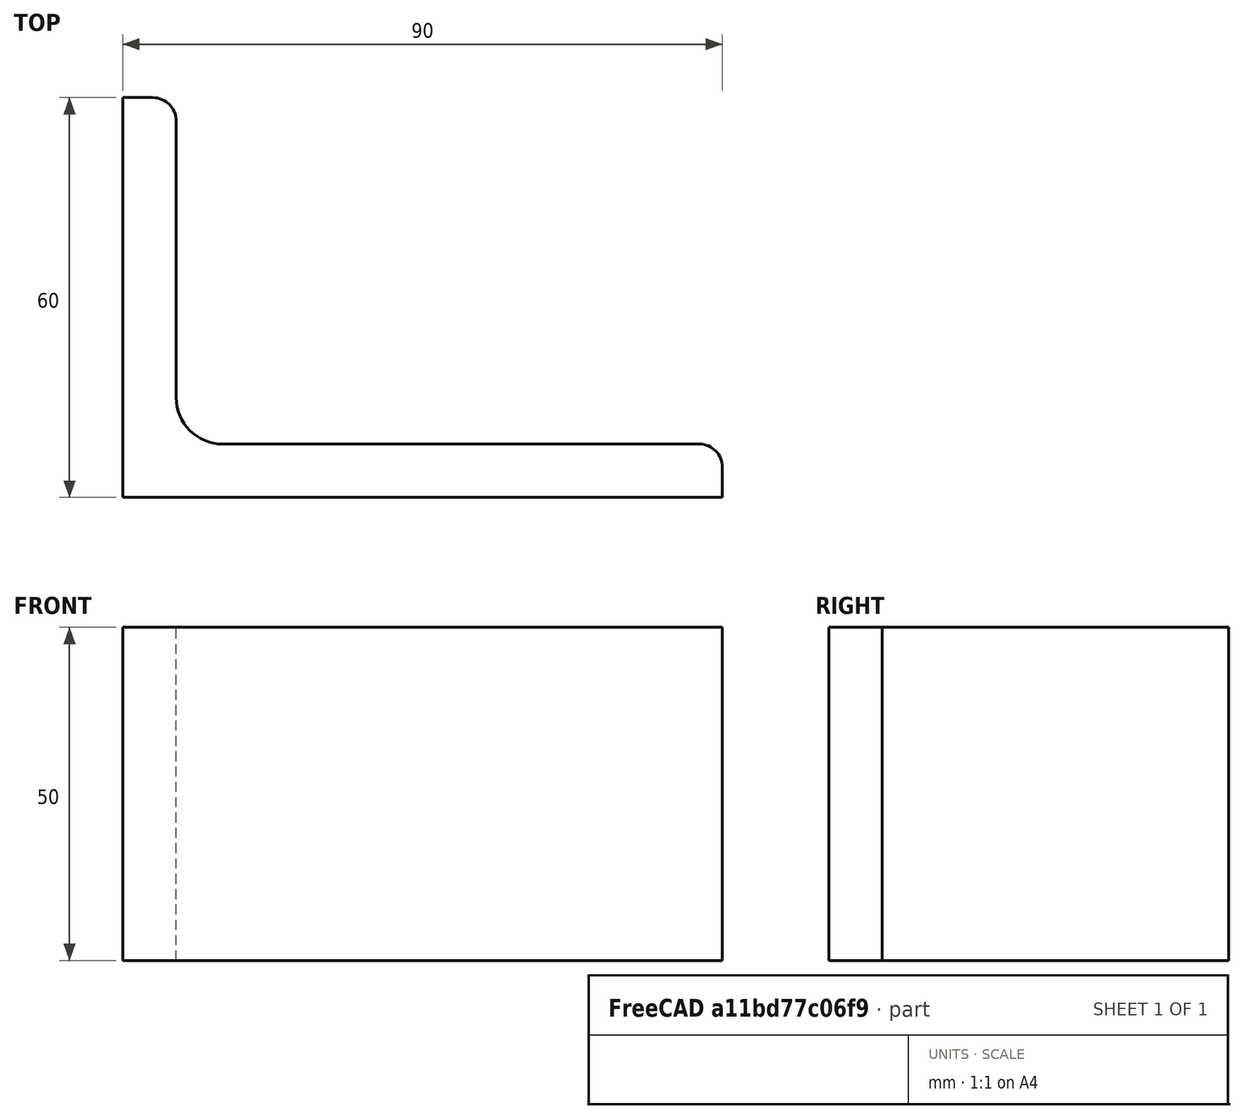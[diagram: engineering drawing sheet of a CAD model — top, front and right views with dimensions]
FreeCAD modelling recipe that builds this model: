
FCSTD DOCUMENT  (FreeCAD 0.15R4671 (Git))
Label: Angle Bar 90x60x8 EN10056 S235JR
License: All rights reserved
LicenseURL: http://en.wikipedia.org/wiki/All_rights_reserved
objects: Sketcher::SketchObject×1, Part::Extrusion×1
note: 2 computed .brp shape members not serialized (recipe doc carries the construction recipe); baked Part::Feature solids carry a one-line shape summary decoded from their .brp

FEATURE [Sketcher::SketchObject] Sketch
  sketch-geometry (9):
    g0: LineSegment StartX=0 StartY=0 StartZ=0 EndX=90 EndY=0 EndZ=0
    g1: LineSegment StartX=90 StartY=0 StartZ=0 EndX=90 EndY=4.5 EndZ=0
    g2: LineSegment StartX=86.5 StartY=8 StartZ=0 EndX=15 EndY=8 EndZ=0
    g3: LineSegment StartX=0 StartY=0 StartZ=0 EndX=0 EndY=60 EndZ=0
    g4: LineSegment StartX=0 StartY=60 StartZ=0 EndX=4.5 EndY=60 EndZ=0
    g5: LineSegment StartX=8 StartY=56.5 StartZ=0 EndX=8 EndY=15 EndZ=0
    g6: ArcOfCircle CenterX=15 CenterY=15 CenterZ=0 NormalX=0 NormalY=0 NormalZ=1 Radius=7 StartAngle=3.14159 EndAngle=4.71239
    g7: ArcOfCircle CenterX=4.5 CenterY=56.5 CenterZ=0 NormalX=0 NormalY=0 NormalZ=1 Radius=3.5 StartAngle=0 EndAngle=1.5708
    g8: ArcOfCircle CenterX=86.5 CenterY=4.5 CenterZ=0 NormalX=0 NormalY=0 NormalZ=1 Radius=3.5 StartAngle=0 EndAngle=1.5708
  constraints (23):
    c: Coincident(g0,g-1)
    c: Horizontal(g0)
    c: Coincident(g1,g0)
    c: Vertical(g1)
    c: Horizontal(g2)
    c: Coincident(g3,g-1)
    c: Vertical(g3)
    c: Coincident(g4,g3)
    c: Horizontal(g4)
    c: Vertical(g5)
    c: Tangent(g5,g6) = -1.5708
    c: Tangent(g2,g6) = 1.5708
    c: Tangent(g4,g7) = 1.5708
    c: Tangent(g5,g7) = 1.5708
    c: Tangent(g2,g8) = -1.5708
    c: Tangent(g1,g8) = -1.5708
    c: DistanceX(g0) = 90
    c: DistanceY(g3) = 60
    c: DistanceY(g0,g2) = 8
    c: DistanceX(g3,g5) = 8
    c: Radius(g6) = 7
    c: Radius(g8) = 3.5
    c: Radius(g7) = 3.5
FEATURE [Part::Extrusion] Extrude  label="Angle Bar 90x60x8 EN10056 S235JR"
  Base = -> Sketch
  Dir = (0,0,50)
  Solid = true
